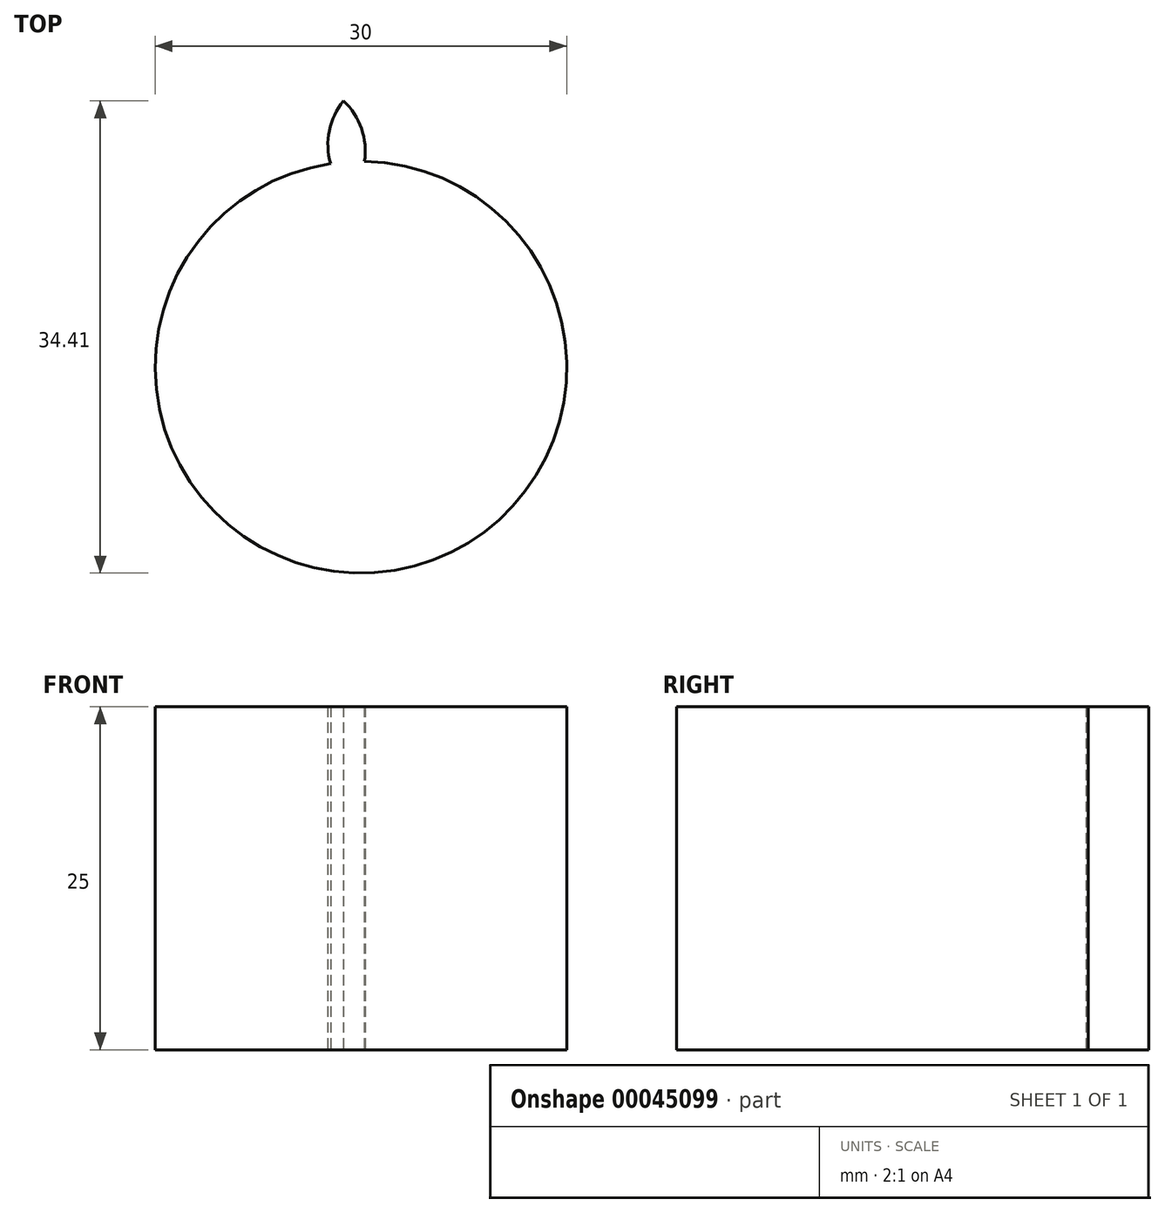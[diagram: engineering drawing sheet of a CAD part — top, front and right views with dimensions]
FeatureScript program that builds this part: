
annotation { "Feature Type Name" : "Feature", "Feature Type Description" : "" }
export const myFeature = defineFeature(function(context is Context, id is Id, definition is map)
    precondition{}
    {
        {
            var Q0;
            Q0=qCreatedBy(makeId("Top.planeOp"),FACE);
            var sketch = newSketch(context, id + "F0", { "sketchPlane" : qUnion([Q0])});
            skCircle(sketch, "E0", {"center": v(0, 0) * mm, "radius": 15 * mm});
            skCircle(sketch, "E1", {"center": v(0, 0) * mm, "radius": 17.5 * mm, "construction": true});
            skCircle(sketch, "E2", {"center": v(0, 0) * mm, "radius": 20 * mm, "construction": true});
            skLineSegment(sketch, "E3", {"start": v(0, 0) * mm, "end": v(0, 28.31) * mm, "construction": true});
            skLineSegment(sketch, "E4", {"start": v(0, 0) * mm, "end": v(-1.83, 27.91) * mm, "construction": true});
            skLineSegment(sketch, "E5", {"start": v(0, 17.5) * mm, "end": v(-43.08, 17.5) * mm, "construction": true});
            skLineSegment(sketch, "E6", {"start": v(0, 17.5) * mm, "end": v(-41.94, 2.24) * mm, "construction": true});
            skCircle(sketch, "E7", {"center": v(0, 17.5) * mm, "radius": 5 * mm, "construction": true});
            skCircle(sketch, "E8", {"center": v(0, 0) * mm, "radius": 16.44 * mm, "construction": true});
            skCircle(sketch, "E9", {"center": v(-4.69, 15.76) * mm, "radius": 5 * mm, "construction": true});
            skArc(sketch, "E10", {"start": v(0.25, 15) * mm, "mid": v(0.04, 17.4) * mm, "end": v(-1.27, 19.41) * mm});
            skArc(sketch, "E11.MirrorCS", {"start": v(-2.2, 14.84) * mm, "mid": v(-2.3, 17.24) * mm, "end": v(-1.27, 19.41) * mm});
            skSolve(sketch);
        }
        {
            var Q0;
            {var subQ1=sQuery(id+"F0.wireOp",EDGE,"E10");Q0=makeQuery(id+"F0.imprint","IMPRINT",FACE,{"disambiguationData":[TD([[makeQuery(id+"F0.imprint","IMPRINT",EDGE,{"derivedFrom":subQ1}),1.0]])]});}
            var Q1;
            {var subQ0=sQuery(id+"F0.wireOp",EDGE,"E0");var subQ2=makeQuery(id+"F0.imprint","INTERSECT",VERTEX,{"derivedFrom":[subQ0,sQuery(id+"F0.wireOp",EDGE,"E10")]});Q1=makeQuery(id+"F0.imprint","IMPRINT",FACE,{"disambiguationData":[TD([[makeQuery(id+"F0.imprint","IMPRINT",EDGE,{"disambiguationData":[TD([[subQ2,-1.0]])],"derivedFrom":subQ0}),1.0]])]});}
            extrude(context, id + "F1", {"entities" : qUnion([Q0, Q1]), "depth" : 25 * mm});
        }
    });
